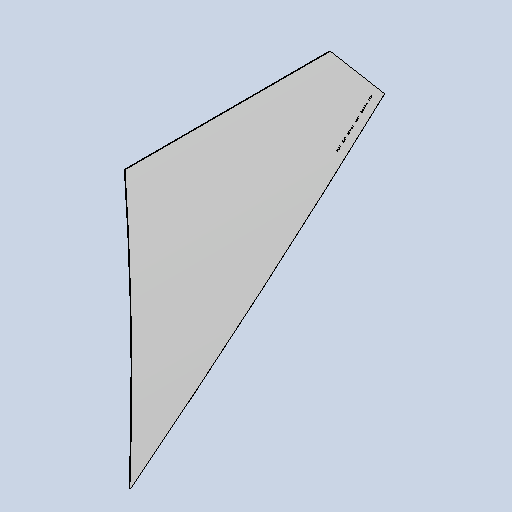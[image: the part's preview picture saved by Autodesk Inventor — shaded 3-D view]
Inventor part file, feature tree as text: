
AUTODESK INVENTOR PART (.ipt)
format: ipt  version: 2025 (Build 290162010, 162A)  size: 489,984 bytes
history: native  units: mm
features: sheet_metal_op x3, other x3, sketch x3, extrude x1, fillet x1, projected_geometry x1
ambient origin geometry x8: Origin, YZ Plane, XZ Plane, XY Plane, X Axis, Y Axis, Z Axis, Center Point
bodies: Body1 (feature_tree)
feature tree (12):
  sheet_metal_op  "Contour Flange2"
  extrude  "Extrusion2"  Depth=3.0mm
  fillet  "Fillet1"  Radius=1.5mm
  other  "Mark1"
  sketch  "Sketch1"  dims[d36=3.0mm d37=3.0mm d38=1.5mm]
  other  "Plate2"
  sheet_metal_op  "Bend2"
  sheet_metal_op  "Corner2"
  sketch  "Sketch2"  dims[d39=6.0mm]
  projected_geometry  "Projected Loop1"
  sketch  "Sketch3"  dims[d40=5.0mm d41=1250.0mm d42=5.0mm d43=3.0mm d44=12.0mm d45=3.0mm d46=5.0mm d54=1500.0mm d55=2700.0mm d58=2100.0mm d65=8.0mm d66=8.0mm d68=8.0mm d69=3.0mm d70=3.0mm d75=3.0mm d78=3.0mm d80=3.0mm d83=8.0mm d86=3.0mm d112=241.9mm d113=50.0mm d114=50.0mm d115=3.0mm d116=25.0mm d117=110.0mm d118=25.0mm d119=92.8mm d130=0.0mm d131=0.0mm d132=8.726646mm d133=1286.0mm d134=3.0mm d135=290.0mm d137=12.0mm d138=200.0mm d139=50.0mm d140=50.0mm]
  other  "Definition1"
